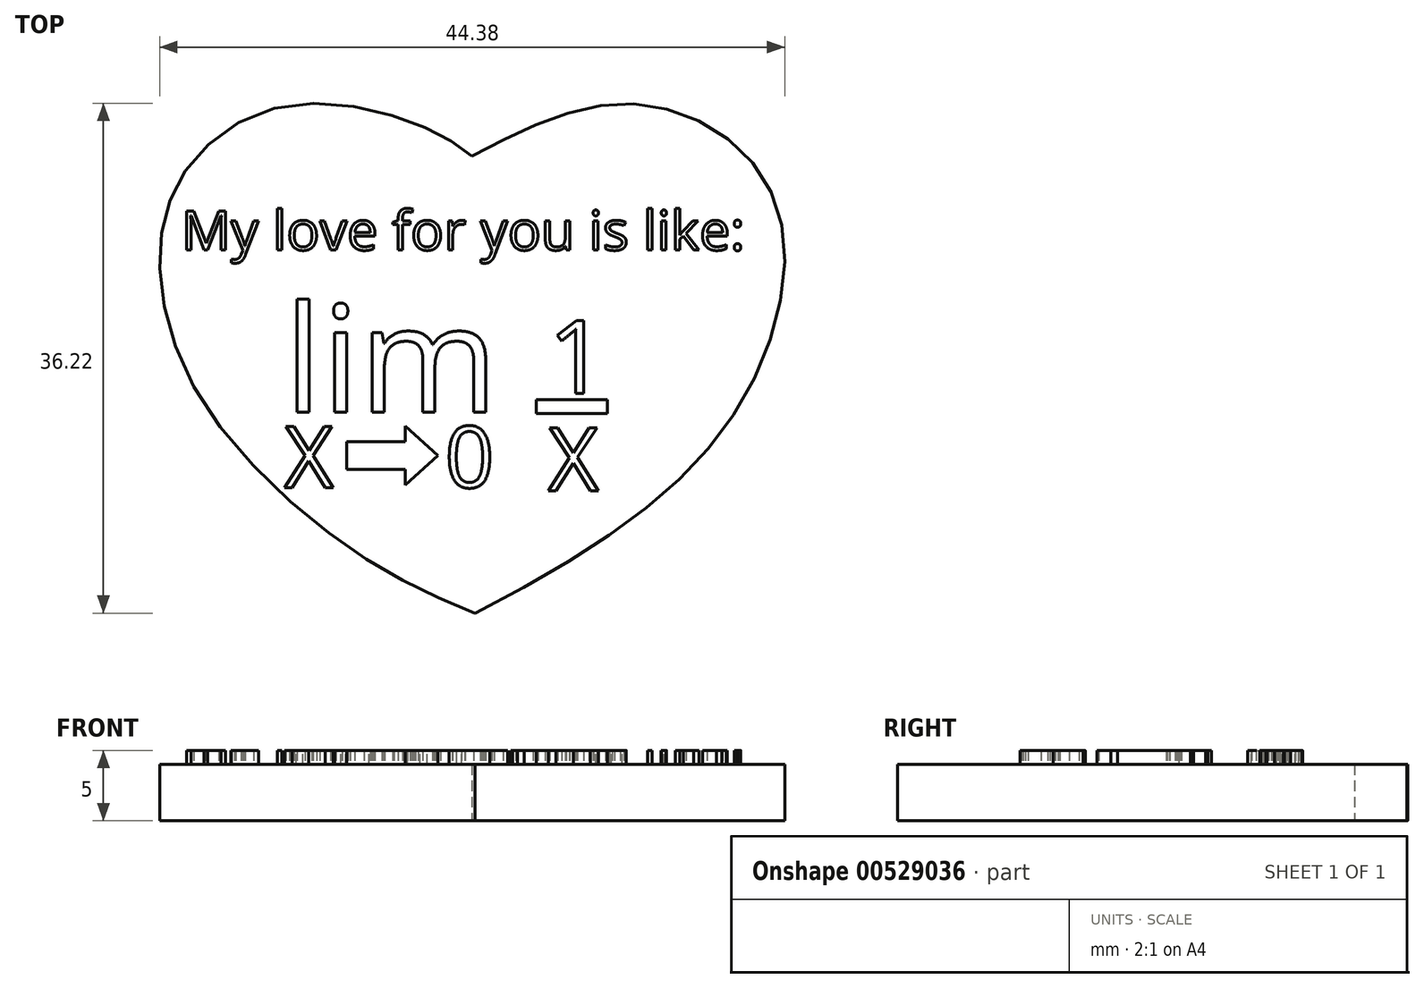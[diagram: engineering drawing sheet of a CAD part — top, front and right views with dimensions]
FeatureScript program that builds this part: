
annotation { "Feature Type Name" : "Feature", "Feature Type Description" : "" }
export const myFeature = defineFeature(function(context is Context, id is Id, definition is map)
    precondition{}
    {
        {
            var Q0;
            Q0=qCreatedBy(makeId("Top.planeOp"),FACE);
            var sketch = newSketch(context, id + "F0", { "sketchPlane" : qUnion([Q0])});
            skFitSpline(sketch, "E0", {"points": [v(49.6, 70.34) * mm, v(73.34, 77.72) * mm, v(92.4, 64.64) * mm, v(87.02, 34) * mm, v(50.07, 5.42) * mm], "startDerivative": vector(104.52, 55.2) * mm, "endDerivative": vector(-164.24, -85.38) * mm});
            skFitSpline(sketch, "E1", {"points": [v(49.6, 70.34) * mm, v(40.98, 75.22) * mm, v(22.79, 77.45) * mm, v(9.23, 68.72) * mm, v(5.28, 55.8) * mm, v(10.9, 36.23) * mm, v(31.88, 14.89) * mm, v(50.07, 5.42) * mm], "startDerivative": vector(-61.26, 53.1) * mm, "endDerivative": vector(123.7, -48.3) * mm});
            skSolve(sketch);
        }
        {
            var Q0;
            Q0=makeQuery(id+"F0.imprint","IMPRINT",FACE,{"disambiguationData":[TD([[makeQuery(id+"F0.imprint","IMPRINT",EDGE,{"derivedFrom":sQuery(id+"F0.wireOp",EDGE,"E0")}),-1.0]])]});
            extrude(context, id + "F1", {"entities" : qUnion([Q0]), "endBound" : BoundingType.SYMMETRIC, "depth" : 8 * mm, "offsetDistance" : 25 * mm});
        }
        {
            var Q0;
            Q0=makeQuery(id+"F1.opExtrude","SWEPT_BODY",BODY,{"disambiguationData":[OSD([sQuery(id+"F0.wireOp",EDGE,"E0"),sQuery(id+"F0.wireOp",EDGE,"E1")])]});
            var Q1;
            Q1=qCreatedBy(makeId("Origin.pointOp"),VERTEX);
            transform(context, id + "F2", {"entities" : qUnion([Q0]), "transformType" : TransformType.SCALE_UNIFORMLY, "scale" : .5, "scalePoint" : qUnion([Q1]), "makeCopy" : false});
        }
        {
            var Q0;
            Q0=qCreatedBy(makeId("Top.planeOp"),FACE);
            var sketch = newSketch(context, id + "F3", { "sketchPlane" : qUnion([Q0])});
            skText(sketch, "E2", { "text": "My love for you is like:\n ", "fontName": "OpenSans-Regular.ttf"});
            skText(sketch, "E3", { "text": "lim", "fontName": "OpenSans-Regular.ttf"});
            skText(sketch, "E4", { "text": "X     0", "fontName": "OpenSans-Regular.ttf"});
            skLineSegment(sketch, "E5", {"start": v(15.9, 14.9) * mm, "end": v(20.07, 14.9) * mm});
            skLineSegment(sketch, "E6", {"start": v(20.07, 14.9) * mm, "end": v(20.07, 16.01) * mm});
            skLineSegment(sketch, "E7", {"start": v(20.07, 16.01) * mm, "end": v(22.4, 13.9) * mm});
            skLineSegment(sketch, "E8.MirrorCS", {"start": v(15.9, 12.9) * mm, "end": v(20.07, 12.9) * mm});
            skLineSegment(sketch, "E9.MirrorCS", {"start": v(20.07, 12.9) * mm, "end": v(20.07, 11.8) * mm});
            skLineSegment(sketch, "E10.MirrorCS", {"start": v(20.07, 11.8) * mm, "end": v(22.4, 13.9) * mm});
            skLineSegment(sketch, "E11", {"start": v(15.9, 14.9) * mm, "end": v(15.9, 12.9) * mm});
            skText(sketch, "E12", { "text": "1", "fontName": "OpenSans-Regular.ttf"});
            skLineSegment(sketch, "E13", {"start": v(29.38, 17.88) * mm, "end": v(29.38, 16.89) * mm});
            skLineSegment(sketch, "E14", {"start": v(29.38, 16.89) * mm, "end": v(34.42, 16.89) * mm});
            skLineSegment(sketch, "E15", {"start": v(29.38, 17.88) * mm, "end": v(34.42, 17.88) * mm});
            skLineSegment(sketch, "E16", {"start": v(34.42, 16.89) * mm, "end": v(34.42, 17.88) * mm});
            skText(sketch, "E17", { "text": "X", "fontName": "OpenSans-Regular.ttf"});
            const initialGuessF3  = {"E2": [0.00418, 0.0285, 1, 0, 0.0028], "E3": [0.01148, 0.017, 1, 0, 0.0076], "E4": [0.01148, 0.01163, 1, 0, 0.00438], "E12": [0.0302, 0.01833, 1, 0, 0.00522], "E17": [0.0302, 0.01141, 1, 0, 0.00451]};
            skSetInitialGuess(sketch, initialGuessF3);
            skSolve(sketch);
        }
        {
            var Q0;
            Q0 = qSketchRegion(id + "F3", true);
            extrude(context, id + "F4", {"entities" : qUnion([Q0]), "operationType" : NewBodyOperationType.ADD, "depth" : 3 * mm, "offsetDistance" : 25 * mm});
        }
    });
